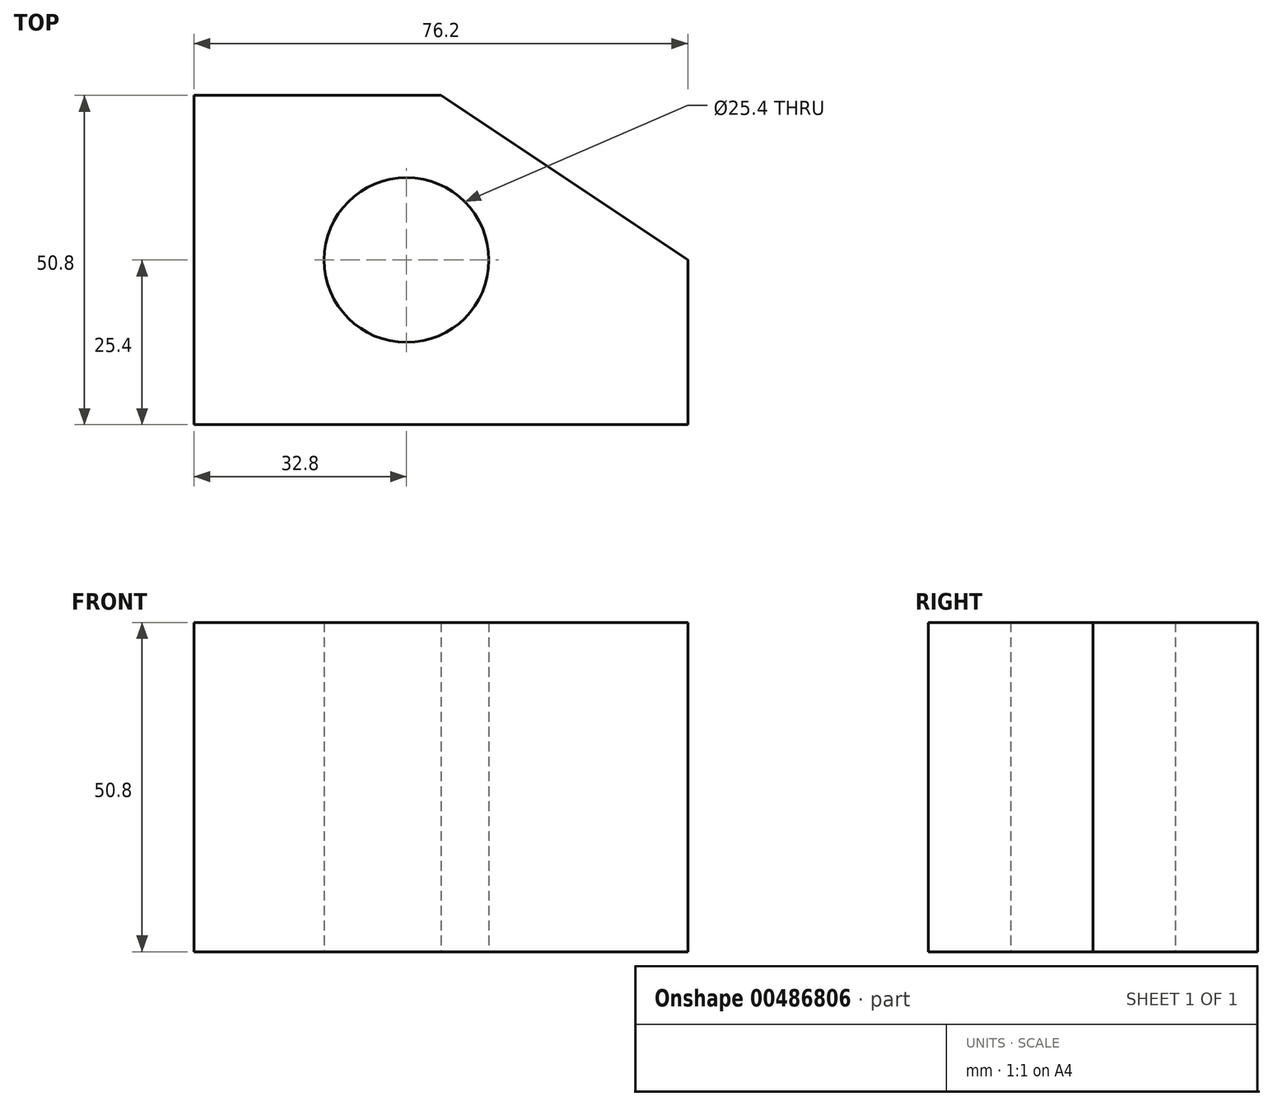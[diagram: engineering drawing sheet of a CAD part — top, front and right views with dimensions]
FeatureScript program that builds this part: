
annotation { "Feature Type Name" : "Feature", "Feature Type Description" : "" }
export const myFeature = defineFeature(function(context is Context, id is Id, definition is map)
    precondition{}
    {
        {
            var Q0;
            Q0=qCreatedBy(makeId("Top.planeOp"),FACE);
            var sketch = newSketch(context, id + "F0", { "sketchPlane" : qUnion([Q0])});
            skLineSegment(sketch, "E0.bottom", {"start": v(0, 0) * mm, "end": v(-38.1, 0) * mm});
            skLineSegment(sketch, "E0.top", {"start": v(0, 50.8) * mm, "end": v(-38.1, 50.8) * mm});
            skLineSegment(sketch, "E0.right", {"start": v(-38.1, 0) * mm, "end": v(-38.1, 50.8) * mm});
            skLineSegment(sketch, "E1.bottom", {"start": v(0, 0) * mm, "end": v(38.1, 0) * mm});
            skLineSegment(sketch, "E1.right", {"start": v(38.1, 0) * mm, "end": v(38.1, 25.4) * mm});
            skLineSegment(sketch, "E2", {"start": v(0, 50.8) * mm, "end": v(38.1, 25.4) * mm});
            skCircle(sketch, "E3", {"center": v(-5.3, 25.4) * mm, "radius": 12.7 * mm});
            skSolve(sketch);
        }
        {
            var Q0;
            Q0 = qSketchRegion(id + "F0", true);
            extrude(context, id + "F1", {"entities" : qUnion([Q0]), "depth" : 50.8 * mm});
        }
    });
